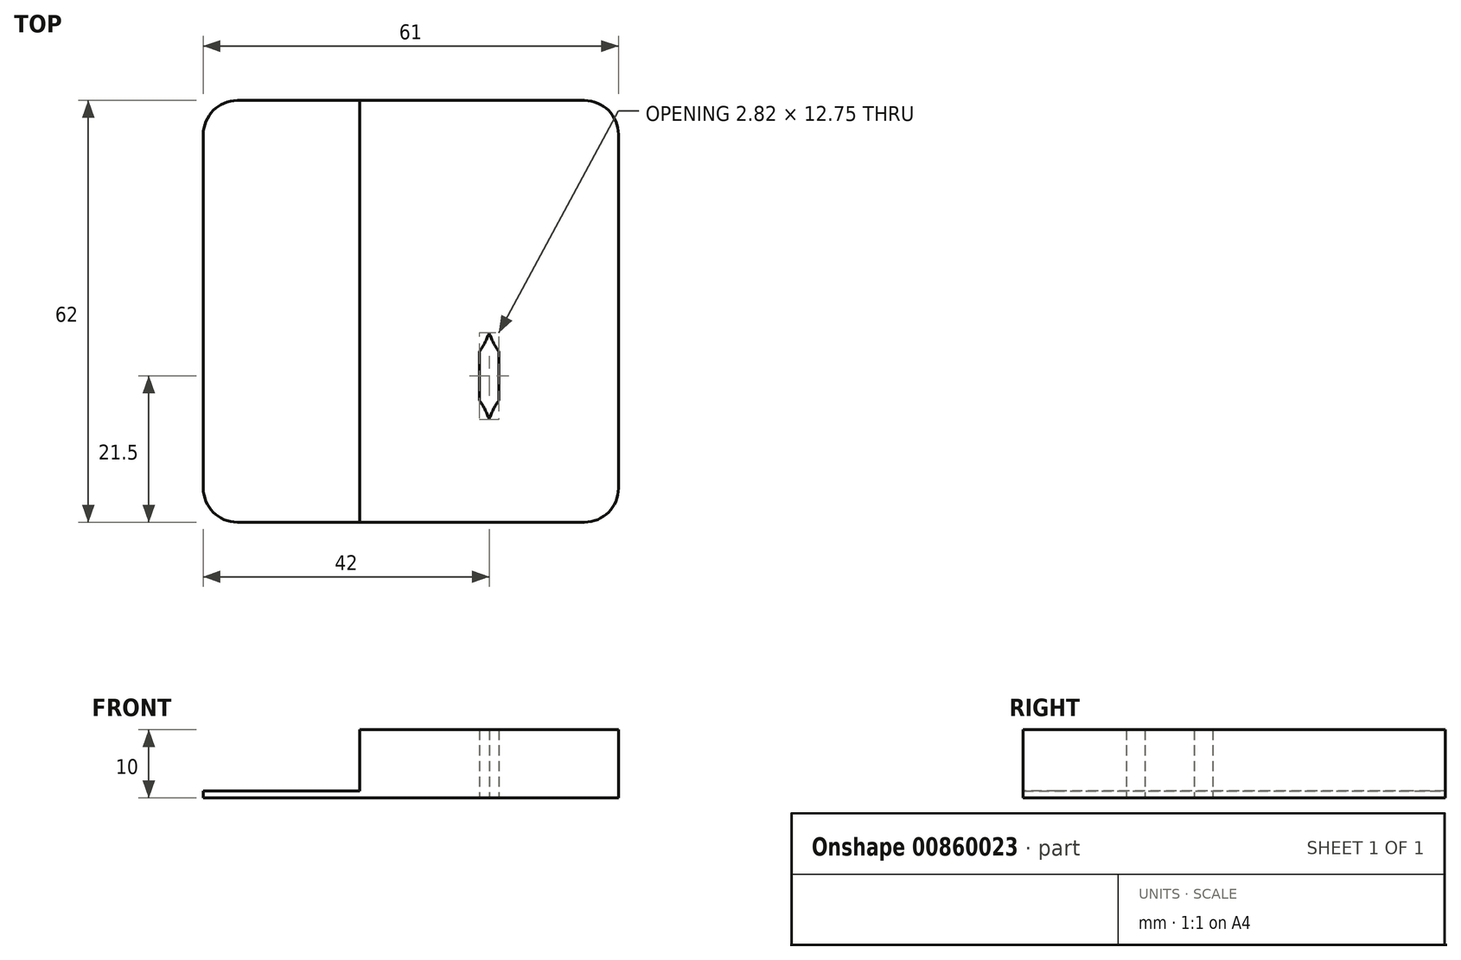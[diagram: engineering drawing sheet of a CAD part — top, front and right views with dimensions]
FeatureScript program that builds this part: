
annotation { "Feature Type Name" : "Feature", "Feature Type Description" : "" }
export const myFeature = defineFeature(function(context is Context, id is Id, definition is map)
    precondition{}
    {
        {
            var Q0;
            Q0=qCreatedBy(makeId("Top.planeOp"),FACE);
            var sketch = newSketch(context, id + "F0", { "sketchPlane" : qUnion([Q0])});
            skLineSegment(sketch, "E0.direction1", {"start": v(0, 0) * mm, "end": v(19, 0) * mm, "construction": true});
            skLineSegment(sketch, "E0.direction2", {"start": v(0, 0) * mm, "end": v(0, 9.5) * mm, "construction": true});
            skLineSegment(sketch, "E1", {"start": v(-61.7, 19) * mm, "end": v(75.9, 19) * mm, "construction": true});
            skLineSegment(sketch, "E2.bottom", {"start": v(28.5, 50) * mm, "end": v(-9.5, 50) * mm});
            skLineSegment(sketch, "E2.top", {"start": v(28.5, -12) * mm, "end": v(-9.5, -12) * mm});
            skLineSegment(sketch, "E2.left", {"start": v(28.5, 50) * mm, "end": v(28.5, -12) * mm});
            skLineSegment(sketch, "E2.right", {"start": v(-9.5, 50) * mm, "end": v(-9.5, -12) * mm});
            skPoint(sketch, "E2.middle", {"position": v(9.5, 19) * mm});
            skLineSegment(sketch, "E3.bottom", {"start": v(-9.5, 50) * mm, "end": v(-32.5, 50) * mm});
            skLineSegment(sketch, "E3.top", {"start": v(-9.5, -12) * mm, "end": v(-32.5, -12) * mm});
            skLineSegment(sketch, "E3.right", {"start": v(-32.5, 50) * mm, "end": v(-32.5, -12) * mm});
            skLineSegment(sketch, "E4", {"start": v(0, 28.5) * mm, "end": v(21.88, 28.5) * mm, "construction": true});
            skLineSegment(sketch, "E5", {"start": v(9.5, 19) * mm, "end": v(9.5, 38.07) * mm, "construction": true});
            skArc(sketch, "E6.0", {"start": v(8.09, 32.12) * mm, "mid": v(8.9, 33.44) * mm, "end": v(9.5, 34.88) * mm});
            skArc(sketch, "E7.0", {"start": v(9.5, 34.88) * mm, "mid": v(10.1, 33.44) * mm, "end": v(10.91, 32.12) * mm});
            skArc(sketch, "E8.0", {"start": v(9.5, 22.12) * mm, "mid": v(8.9, 23.56) * mm, "end": v(8.09, 24.88) * mm});
            skArc(sketch, "E9.0", {"start": v(10.91, 24.88) * mm, "mid": v(10.1, 23.56) * mm, "end": v(9.5, 22.12) * mm});
            skLineSegment(sketch, "E10", {"start": v(10.91, 32.12) * mm, "end": v(10.91, 24.88) * mm});
            skLineSegment(sketch, "E11.MirrorCS", {"start": v(8.09, 32.12) * mm, "end": v(8.09, 24.88) * mm});
            skArc(sketch, "E12.MirrorCS", {"start": v(10.91, 13.12) * mm, "mid": v(10.1, 14.44) * mm, "end": v(9.5, 15.88) * mm});
            skArc(sketch, "E13.MirrorCS", {"start": v(9.5, 15.88) * mm, "mid": v(8.9, 14.44) * mm, "end": v(8.09, 13.12) * mm});
            skLineSegment(sketch, "E14.MirrorCS", {"start": v(10.91, 5.88) * mm, "end": v(10.91, 13.12) * mm});
            skLineSegment(sketch, "E15.MirrorCS", {"start": v(8.09, 5.88) * mm, "end": v(8.09, 13.12) * mm});
            skArc(sketch, "E16.MirrorCS", {"start": v(8.09, 5.88) * mm, "mid": v(8.9, 4.56) * mm, "end": v(9.5, 3.12) * mm});
            skArc(sketch, "E17.MirrorCS", {"start": v(9.5, 3.12) * mm, "mid": v(10.1, 4.56) * mm, "end": v(10.91, 5.88) * mm});
            skSolve(sketch);
        }
        {
            var Q0;
            {var subQ5=sQuery(id+"F0.wireOp",EDGE,"wYq4wZY3-02EK-ydR4-tfFt-3672jDLh7bw5");Q0=makeQuery(id+"F0.imprint","IMPRINT",FACE,{"disambiguationData":[TD([[makeQuery(id+"F0.imprint","IMPRINT",EDGE,{"derivedFrom":subQ5}),1.0]])]});}
            var Q1;
            {var subQ0=sQuery(id+"F0.wireOp",EDGE,"E0.0.2.0");Q1=makeQuery(id+"F0.imprint","IMPRINT",FACE,{"disambiguationData":[TD([[makeQuery(id+"F0.imprint","IMPRINT",EDGE,{"derivedFrom":subQ0}),-1.0]])]});}
            var Q2;
            {var subQ0=sQuery(id+"F0.wireOp",EDGE,"wYq4wZY3-02EK-ydR4-tfFt-3672jDLh7bw5");Q2=makeQuery(id+"F0.imprint","IMPRINT",FACE,{"disambiguationData":[TD([[makeQuery(id+"F0.imprint","IMPRINT",EDGE,{"derivedFrom":subQ0}),-1.0]])]});}
            var Q3;
            Q3=makeQuery(id+"F0.imprint","IMPRINT",FACE,{"disambiguationData":[TD([[makeQuery(id+"F0.imprint","IMPRINT",EDGE,{"derivedFrom":sQuery(id+"F0.wireOp",EDGE,"E3.bottom")}),1.0]])]});
            var Q4;
            Q4=makeQuery(id+"F0.imprint","IMPRINT",FACE,{"disambiguationData":[TD([[makeQuery(id+"F0.imprint","IMPRINT",EDGE,{"derivedFrom":sQuery(id+"F0.wireOp",EDGE,"E2.bottom")}),1.0]])]});
            extrude(context, id + "F1", {"entities" : qUnion([Q0, Q1, Q2, Q3, Q4]), "depth" : 1 * mm, "offsetDistance" : 25 * mm});
        }
        {
            var Q0;
            Q0=makeQuery(id+"F0.imprint","IMPRINT",FACE,{"disambiguationData":[TD([[makeQuery(id+"F0.imprint","IMPRINT",EDGE,{"derivedFrom":sQuery(id+"F0.wireOp",EDGE,"E6.0")}),-1.0]])]});
            var Q1;
            Q1=makeQuery(id+"F0.imprint","IMPRINT",FACE,{"disambiguationData":[TD([[makeQuery(id+"F0.imprint","IMPRINT",EDGE,{"derivedFrom":sQuery(id+"F0.wireOp",EDGE,"E12.MirrorCS")}),1.0]])]});
            extrude(context, id + "F2", {"entities" : qUnion([Q0, Q1]), "operationType" : NewBodyOperationType.ADD, "depth" : 10 * mm, "offsetDistance" : 25 * mm});
        }
        {
            var Q0;
            Q0=makeQuery(id+"F1.opExtrude","SWEPT_EDGE",EDGE,{"disambiguationData":[OSD([sQuery(id+"F0.wireOp",EDGE,"E3.bottom"),sQuery(id+"F0.wireOp",EDGE,"E3.right")])]});
            var Q1;
            Q1=makeQuery(id+"F1.opExtrude","SWEPT_EDGE",EDGE,{"disambiguationData":[OSD([sQuery(id+"F0.wireOp",EDGE,"E2.bottom"),sQuery(id+"F0.wireOp",EDGE,"E2.left")])]});
            var Q2;
            Q2=makeQuery(id+"F1.opExtrude","SWEPT_EDGE",EDGE,{"disambiguationData":[OSD([sQuery(id+"F0.wireOp",EDGE,"E2.top"),sQuery(id+"F0.wireOp",EDGE,"E2.left")])]});
            var Q3;
            Q3=makeQuery(id+"F1.opExtrude","SWEPT_EDGE",EDGE,{"disambiguationData":[OSD([sQuery(id+"F0.wireOp",EDGE,"E3.top"),sQuery(id+"F0.wireOp",EDGE,"E3.right")])]});
            fillet(context, id + "F3", {"entities" : qUnion([Q0, Q1, Q2, Q3]), "radius" : 5 * mm, "tangentPropagation" : true, "allowEdgeOverflow" : false});
        }
    });
